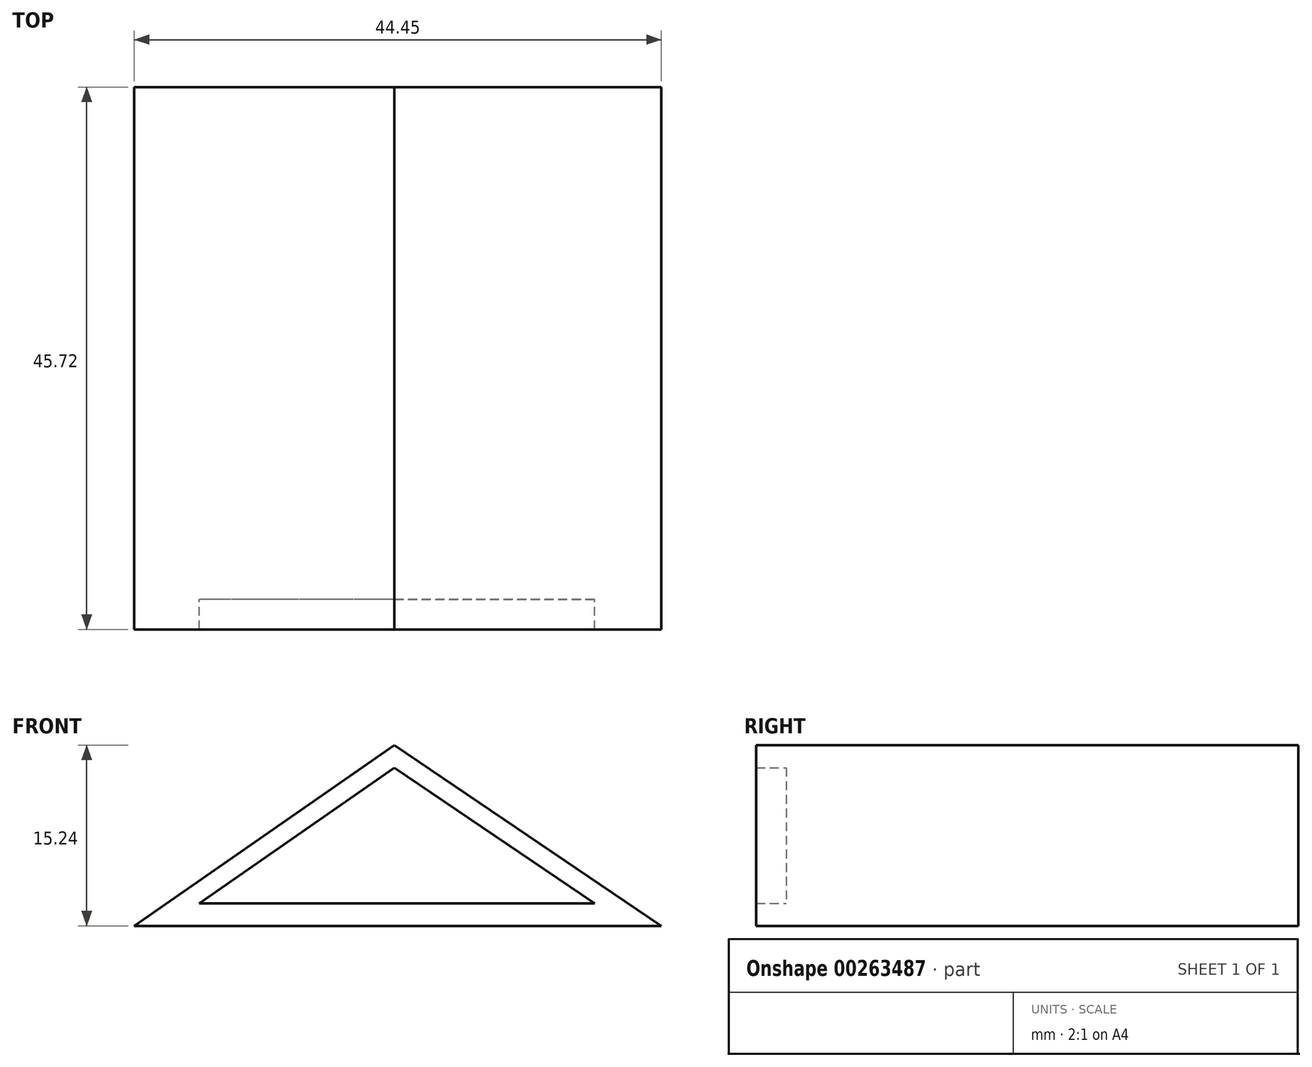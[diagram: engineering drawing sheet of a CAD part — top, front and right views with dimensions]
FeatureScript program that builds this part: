
annotation { "Feature Type Name" : "Feature", "Feature Type Description" : "" }
export const myFeature = defineFeature(function(context is Context, id is Id, definition is map)
    precondition{}
    {
        {
            var Q0;
            Q0=qCreatedBy(makeId("Front.planeOp"),FACE);
            var sketch = newSketch(context, id + "F0", { "sketchPlane" : qUnion([Q0])});
            skLineSegment(sketch, "E0", {"start": v(-21.93, 0) * mm, "end": v(22.52, 0) * mm});
            skLineSegment(sketch, "E1", {"start": v(-21.93, 0) * mm, "end": v(0, 15.24) * mm});
            skLineSegment(sketch, "E2", {"start": v(0, 15.24) * mm, "end": v(22.52, 0) * mm});
            skLineSegment(sketch, "E3", {"start": v(0, 15.24) * mm, "end": v(0, 13.33) * mm});
            skLineSegment(sketch, "E4", {"start": v(0, 13.33) * mm, "end": v(-16.45, 1.9) * mm});
            skLineSegment(sketch, "E5", {"start": v(0, 13.33) * mm, "end": v(16.89, 1.9) * mm});
            skLineSegment(sketch, "E6", {"start": v(0, 0) * mm, "end": v(0, 1.9) * mm});
            skLineSegment(sketch, "E7", {"start": v(0, 1.9) * mm, "end": v(-16.45, 1.9) * mm});
            skLineSegment(sketch, "E8", {"start": v(0, 1.9) * mm, "end": v(16.89, 1.9) * mm});
            skSolve(sketch);
        }
        {
            var Q0;
            Q0 = qSketchRegion(id + "F0", true);
            extrude(context, id + "F1", {"entities" : qUnion([Q0]), "depth" : 45.72 * mm});
        }
        {
            var Q0;
            Q0=makeQuery(id+"F0.imprint","IMPRINT",FACE,{"disambiguationData":[TD([[makeQuery(id+"F0.imprint","IMPRINT",EDGE,{"derivedFrom":sQuery(id+"F0.wireOp",EDGE,"E4")}),1.0]])]});
            extrude(context, id + "F2", {"entities" : qUnion([Q0]), "operationType" : NewBodyOperationType.ADD, "depth" : 43.18 * mm});
        }
    });
